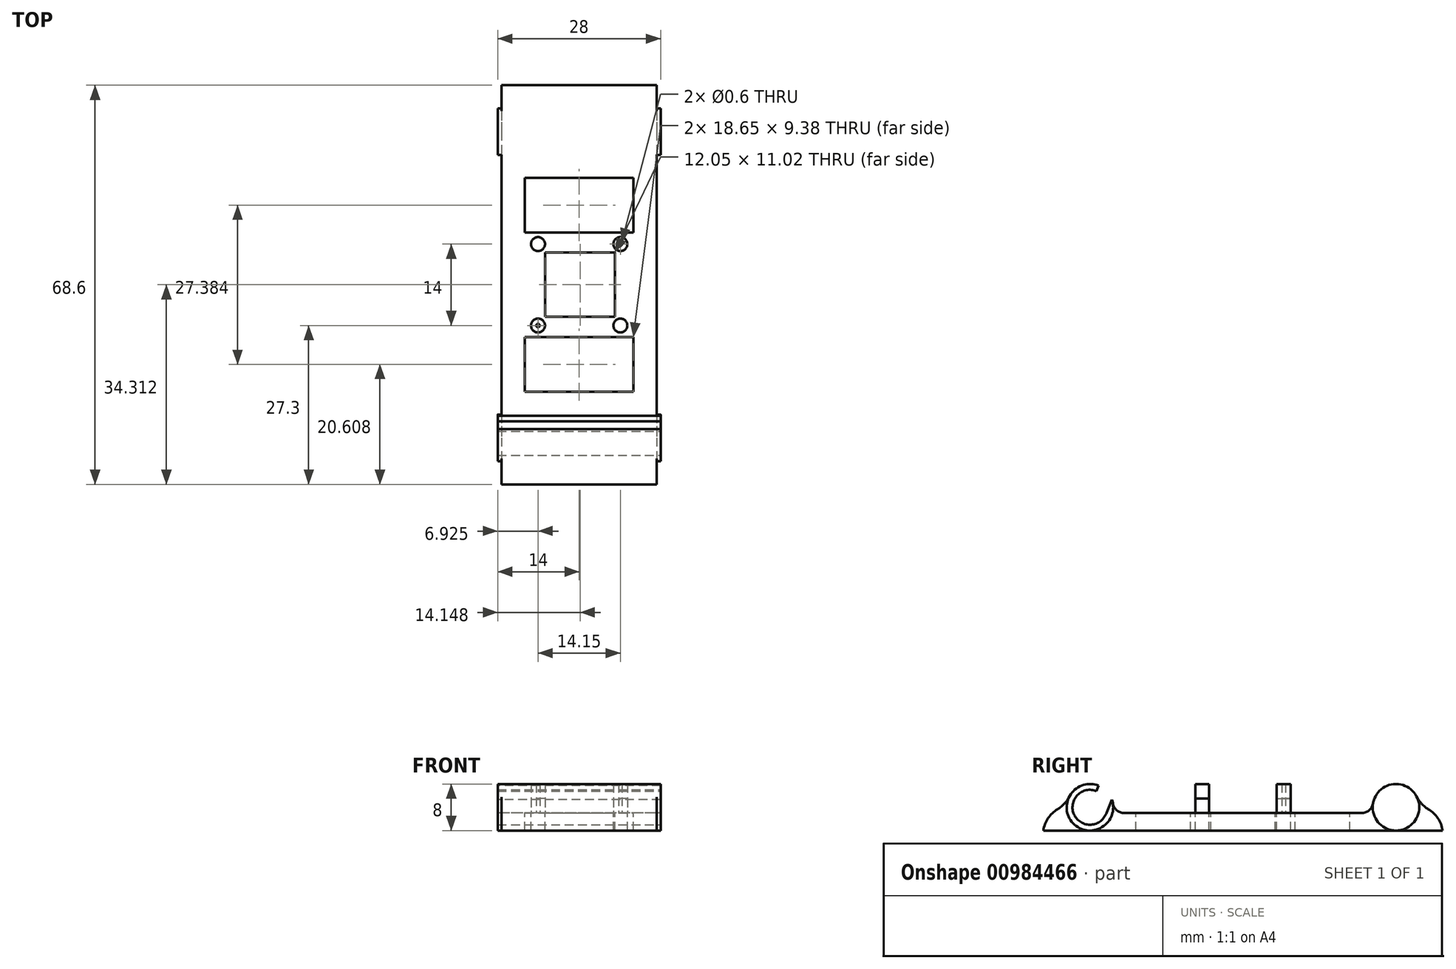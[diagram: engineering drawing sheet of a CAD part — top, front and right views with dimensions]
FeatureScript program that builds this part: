
annotation { "Feature Type Name" : "Feature", "Feature Type Description" : "" }
export const myFeature = defineFeature(function(context is Context, id is Id, definition is map)
    precondition{}
    {
        {
            var Q0;
            Q0=qCreatedBy(makeId("Top.planeOp"),FACE);
            var sketch = newSketch(context, id + "F0", { "sketchPlane" : qUnion([Q0])});
            skCircle(sketch, "E0", {"center": v(7.08, 7) * mm, "radius": 1.2 * mm});
            skLineSegment(sketch, "E1", {"start": v(7.08, 7) * mm, "end": v(-7.08, 7) * mm, "construction": true});
            skCircle(sketch, "E2", {"center": v(-7.07, -7) * mm, "radius": 1.2 * mm});
            skLineSegment(sketch, "E3", {"start": v(7.08, 7) * mm, "end": v(7.08, -7) * mm, "construction": true});
            skLineSegment(sketch, "E4", {"start": v(-7.08, 7) * mm, "end": v(-7.08, -7) * mm, "construction": true});
            skLineSegment(sketch, "E5", {"start": v(-7.07, -7) * mm, "end": v(7.08, -7) * mm, "construction": true});
            skSolve(sketch);
        }
        {
            var Q0;
            Q0 = qSketchRegion(id + "F0", true);
            extrude(context, id + "F1", {"entities" : qUnion([Q0]), "depth" : 5 * mm, "offsetDistance" : 25 * mm});
        }
        {
            var Q0;
            Q0=qCreatedBy(makeId("Top.planeOp"),FACE);
            var sketch = newSketch(context, id + "F2", { "sketchPlane" : qUnion([Q0])});
            skCircle(sketch, "E6", {"center": v(-7.08, -7) * mm, "radius": 0.3 * mm});
            skCircle(sketch, "E7", {"center": v(7.08, 7) * mm, "radius": 0.3 * mm});
            skSolve(sketch);
        }
        {
            var Q0;
            Q0 = qSketchRegion(id + "F2", true);
            extrude(context, id + "F3", {"entities" : qUnion([Q0]), "operationType" : NewBodyOperationType.REMOVE, "depth" : 5 * mm, "offsetDistance" : 25 * mm});
        }
        {
            var Q0;
            Q0=qCreatedBy(makeId("Top.planeOp"),FACE);
            var sketch = newSketch(context, id + "F4", { "sketchPlane" : qUnion([Q0])});
            skLineSegment(sketch, "E8", {"start": v(-8.33, -8.25) * mm, "end": v(-8.33, 8.25) * mm});
            skLineSegment(sketch, "E9", {"start": v(-8.33, 8.25) * mm, "end": v(8.32, 8.25) * mm});
            skLineSegment(sketch, "E10", {"start": v(8.33, -8.25) * mm, "end": v(-8.32, -8.25) * mm});
            skLineSegment(sketch, "E11", {"start": v(8.33, -8.25) * mm, "end": v(8.33, 8.25) * mm});
            skLineSegment(sketch, "E12.bottom", {"start": v(-5.88, -5.5) * mm, "end": v(6.17, -5.5) * mm});
            skLineSegment(sketch, "E12.top", {"start": v(-5.88, 5.52) * mm, "end": v(6.17, 5.52) * mm});
            skLineSegment(sketch, "E12.left", {"start": v(-5.88, -5.5) * mm, "end": v(-5.88, 5.52) * mm});
            skLineSegment(sketch, "E12.right", {"start": v(6.17, -5.5) * mm, "end": v(6.17, 5.52) * mm});
            skSolve(sketch);
        }
        {
            var Q0;
            Q0 = qSketchRegion(id + "F4", true);
            extrude(context, id + "F5", {"entities" : qUnion([Q0]), "oppositeDirection" : true, "depth" : 3 * mm, "offsetDistance" : 25 * mm});
        }
        {
            var Q0;
            Q0 = qSketchRegion(id + "F0", true);
            extrude(context, id + "F6", {"entities" : qUnion([Q0]), "oppositeDirection" : true, "depth" : 3 * mm, "offsetDistance" : 25 * mm});
        }
        {
            var Q0;
            Q0=qCreatedBy(makeId("Top.planeOp"),FACE);
            var sketch = newSketch(context, id + "F7", { "sketchPlane" : qUnion([Q0])});
            skCircle(sketch, "E13", {"center": v(-7.08, 7) * mm, "radius": 1.2 * mm});
            skCircle(sketch, "E14", {"center": v(7.08, -7) * mm, "radius": 1.2 * mm});
            skSolve(sketch);
        }
        {
            var Q0;
            Q0 = qSketchRegion(id + "F7", true);
            extrude(context, id + "F8", {"entities" : qUnion([Q0]), "operationType" : NewBodyOperationType.ADD, "depth" : 2.5 * mm, "offsetDistance" : 25 * mm});
        }
        {
            var Q0;
            Q0=qCreatedBy(makeId("Top.planeOp"),FACE);
            var sketch = newSketch(context, id + "F9", { "sketchPlane" : qUnion([Q0])});
            skLineSegment(sketch, "E15.bottom", {"start": v(-8.33, 8.25) * mm, "end": v(8.32, 8.25) * mm});
            skLineSegment(sketch, "E15.top", {"start": v(-8.33, 26.3) * mm, "end": v(8.33, 26.3) * mm, "construction": true});
            skLineSegment(sketch, "E16.bottom", {"start": v(-8.33, -8.25) * mm, "end": v(8.33, -8.25) * mm});
            skLineSegment(sketch, "E17.left", {"start": v(8.32, 8.25) * mm, "end": v(8.32, -8.25) * mm});
            skLineSegment(sketch, "E17.right", {"start": v(13.33, 34.3) * mm, "end": v(13.33, -34.3) * mm});
            skLineSegment(sketch, "E18.right", {"start": v(-13.33, 34.3) * mm, "end": v(-13.32, -34.3) * mm});
            skLineSegment(sketch, "E19", {"start": v(-8.33, 8.25) * mm, "end": v(-8.33, -8.25) * mm});
            skLineSegment(sketch, "E20", {"start": v(-13.33, 34.3) * mm, "end": v(13.33, 34.3) * mm});
            skLineSegment(sketch, "E21", {"start": v(-8.33, -26.3) * mm, "end": v(7.82, -26.3) * mm, "construction": true});
            skLineSegment(sketch, "E22", {"start": v(-13.32, -34.3) * mm, "end": v(13.33, -34.3) * mm});
            skSolve(sketch);
        }
        {
            var Q0;
            Q0 = qSketchRegion(id + "F9", true);
            extrude(context, id + "F10", {"entities" : qUnion([Q0]), "operationType" : NewBodyOperationType.ADD, "oppositeDirection" : true, "depth" : 3 * mm, "offsetDistance" : 25 * mm});
        }
        {
            var Q0;
            Q0=qCreatedBy(makeId("Right.planeOp"),FACE);
            var sketch = newSketch(context, id + "F11", { "sketchPlane" : qUnion([Q0])});
            skLineSegment(sketch, "E23", {"start": v(-26.3, 1) * mm, "end": v(-26.3, 0) * mm, "construction": true});
            skCircle(sketch, "E24", {"center": v(-26.3, 1) * mm, "radius": 4 * mm});
            skLineSegment(sketch, "E25", {"start": v(26.3, 1) * mm, "end": v(26.3, 0) * mm, "construction": true});
            skCircle(sketch, "E26", {"center": v(26.3, 1) * mm, "radius": 4 * mm});
            skSolve(sketch);
        }
        {
            var Q0;
            Q0 = qSketchRegion(id + "F11", true);
            extrude(context, id + "F12", {"entities" : qUnion([Q0]), "operationType" : NewBodyOperationType.ADD, "depth" : 14 * mm, "offsetDistance" : 25 * mm, "hasSecondDirection" : true, "secondDirectionOppositeDirection" : true, "secondDirectionDepth" : 14 * mm});
        }
        {
            var Q0;
            Q0=qCreatedBy(makeId("Right.planeOp"),FACE);
            var sketch = newSketch(context, id + "F13", { "sketchPlane" : qUnion([Q0])});
            skArc(sketch, "E27", {"start": v(-25.17, 3.78) * mm, "mid": v(-29.01, -0.28) * mm, "end": v(-23.44, 0.11) * mm});
            skLineSegment(sketch, "E28", {"start": v(-26.3, 1) * mm, "end": v(-26.3, 0) * mm, "construction": true});
            skLineSegment(sketch, "E29", {"start": v(-24.4, 5.63) * mm, "end": v(-21.63, 4.48) * mm});
            skLineSegment(sketch, "E30", {"start": v(-21.63, 4.48) * mm, "end": v(-23.44, 0.11) * mm});
            skLineSegment(sketch, "E31", {"start": v(-24.4, 5.63) * mm, "end": v(-25.17, 3.78) * mm});
            skSolve(sketch);
        }
        {
            var Q0;
            Q0 = qSketchRegion(id + "F13", true);
            extrude(context, id + "F14", {"entities" : qUnion([Q0]), "operationType" : NewBodyOperationType.REMOVE, "oppositeDirection" : true, "depth" : 14 * mm, "offsetDistance" : 25 * mm, "hasSecondDirection" : true, "secondDirectionOppositeDirection" : false, "secondDirectionDepth" : 14 * mm});
        }
        {
            var Q0;
            Q0=makeQuery(id+"F12.boolean.opBoolean","INTERSECT",EDGE,{"disambiguationData":[OD(0.0)],"derivedFrom":[makeQuery(id+"F10.boolean.opBoolean","MERGE",FACE,{"derivedFrom":[makeQuery(id+"F5.opExtrude","CAP_FACE",FACE,{"disambiguationData":[OSD([sQuery(id+"F4.wireOp",EDGE,"E8"),sQuery(id+"F4.wireOp",EDGE,"E9"),sQuery(id+"F4.wireOp",EDGE,"E10"),sQuery(id+"F4.wireOp",EDGE,"E11"),sQuery(id+"F4.wireOp",EDGE,"E12.bottom"),sQuery(id+"F4.wireOp",EDGE,"E12.top"),sQuery(id+"F4.wireOp",EDGE,"E12.left"),sQuery(id+"F4.wireOp",EDGE,"E12.right")])],"isStart":true}),makeQuery(id+"F10.opExtrude","CAP_FACE",FACE,{"disambiguationData":[OSD([sQuery(id+"F9.wireOp",EDGE,"E15.bottom"),sQuery(id+"F9.wireOp",EDGE,"E16.bottom"),sQuery(id+"F9.wireOp",EDGE,"E17.left"),sQuery(id+"F9.wireOp",EDGE,"E17.right"),sQuery(id+"F9.wireOp",EDGE,"E18.right"),sQuery(id+"F9.wireOp",EDGE,"E19"),sQuery(id+"F9.wireOp",EDGE,"E20"),sQuery(id+"F9.wireOp",EDGE,"E22")])],"isStart":true})]}),makeQuery(id+"F12.opExtrude","SWEPT_FACE",FACE,{"disambiguationData":[OSD([sQuery(id+"F11.wireOp",EDGE,"E24")])]})]});
            var Q1;
            Q1=makeQuery(id+"F12.boolean.opBoolean","INTERSECT",EDGE,{"disambiguationData":[OD(0.0)],"derivedFrom":[makeQuery(id+"F10.boolean.opBoolean","MERGE",FACE,{"derivedFrom":[makeQuery(id+"F5.opExtrude","CAP_FACE",FACE,{"disambiguationData":[OSD([sQuery(id+"F4.wireOp",EDGE,"E8"),sQuery(id+"F4.wireOp",EDGE,"E9"),sQuery(id+"F4.wireOp",EDGE,"E10"),sQuery(id+"F4.wireOp",EDGE,"E11"),sQuery(id+"F4.wireOp",EDGE,"E12.bottom"),sQuery(id+"F4.wireOp",EDGE,"E12.top"),sQuery(id+"F4.wireOp",EDGE,"E12.left"),sQuery(id+"F4.wireOp",EDGE,"E12.right")])],"isStart":true}),makeQuery(id+"F10.opExtrude","CAP_FACE",FACE,{"disambiguationData":[OSD([sQuery(id+"F9.wireOp",EDGE,"E15.bottom"),sQuery(id+"F9.wireOp",EDGE,"E16.bottom"),sQuery(id+"F9.wireOp",EDGE,"E17.left"),sQuery(id+"F9.wireOp",EDGE,"E17.right"),sQuery(id+"F9.wireOp",EDGE,"E18.right"),sQuery(id+"F9.wireOp",EDGE,"E19"),sQuery(id+"F9.wireOp",EDGE,"E20"),sQuery(id+"F9.wireOp",EDGE,"E22")])],"isStart":true})]}),makeQuery(id+"F12.opExtrude","SWEPT_FACE",FACE,{"disambiguationData":[OSD([sQuery(id+"F11.wireOp",EDGE,"E26")])]})]});
            fillet(context, id + "F15", {"entities" : qUnion([Q0, Q1]), "radius" : 5 * mm, "tangentPropagation" : true, "allowEdgeOverflow" : false});
        }
        {
            var Q0;
            Q0=makeQuery(id+"F12.boolean.opBoolean","INTERSECT",EDGE,{"disambiguationData":[OD(1.0)],"derivedFrom":[makeQuery(id+"F10.boolean.opBoolean","MERGE",FACE,{"derivedFrom":[makeQuery(id+"F5.opExtrude","CAP_FACE",FACE,{"disambiguationData":[OSD([sQuery(id+"F4.wireOp",EDGE,"E8"),sQuery(id+"F4.wireOp",EDGE,"E9"),sQuery(id+"F4.wireOp",EDGE,"E10"),sQuery(id+"F4.wireOp",EDGE,"E11"),sQuery(id+"F4.wireOp",EDGE,"E12.bottom"),sQuery(id+"F4.wireOp",EDGE,"E12.top"),sQuery(id+"F4.wireOp",EDGE,"E12.left"),sQuery(id+"F4.wireOp",EDGE,"E12.right")])],"isStart":true}),makeQuery(id+"F10.opExtrude","CAP_FACE",FACE,{"disambiguationData":[OSD([sQuery(id+"F9.wireOp",EDGE,"E15.bottom"),sQuery(id+"F9.wireOp",EDGE,"E16.bottom"),sQuery(id+"F9.wireOp",EDGE,"E17.left"),sQuery(id+"F9.wireOp",EDGE,"E17.right"),sQuery(id+"F9.wireOp",EDGE,"E18.right"),sQuery(id+"F9.wireOp",EDGE,"E19"),sQuery(id+"F9.wireOp",EDGE,"E20"),sQuery(id+"F9.wireOp",EDGE,"E22")])],"isStart":true})]}),makeQuery(id+"F12.opExtrude","SWEPT_FACE",FACE,{"disambiguationData":[OSD([sQuery(id+"F11.wireOp",EDGE,"E24")])]})]});
            var Q1;
            Q1=makeQuery(id+"F12.boolean.opBoolean","INTERSECT",EDGE,{"disambiguationData":[OD(1.0)],"derivedFrom":[makeQuery(id+"F10.boolean.opBoolean","MERGE",FACE,{"derivedFrom":[makeQuery(id+"F5.opExtrude","CAP_FACE",FACE,{"disambiguationData":[OSD([sQuery(id+"F4.wireOp",EDGE,"E8"),sQuery(id+"F4.wireOp",EDGE,"E9"),sQuery(id+"F4.wireOp",EDGE,"E10"),sQuery(id+"F4.wireOp",EDGE,"E11"),sQuery(id+"F4.wireOp",EDGE,"E12.bottom"),sQuery(id+"F4.wireOp",EDGE,"E12.top"),sQuery(id+"F4.wireOp",EDGE,"E12.left"),sQuery(id+"F4.wireOp",EDGE,"E12.right")])],"isStart":true}),makeQuery(id+"F10.opExtrude","CAP_FACE",FACE,{"disambiguationData":[OSD([sQuery(id+"F9.wireOp",EDGE,"E15.bottom"),sQuery(id+"F9.wireOp",EDGE,"E16.bottom"),sQuery(id+"F9.wireOp",EDGE,"E17.left"),sQuery(id+"F9.wireOp",EDGE,"E17.right"),sQuery(id+"F9.wireOp",EDGE,"E18.right"),sQuery(id+"F9.wireOp",EDGE,"E19"),sQuery(id+"F9.wireOp",EDGE,"E20"),sQuery(id+"F9.wireOp",EDGE,"E22")])],"isStart":true})]}),makeQuery(id+"F12.opExtrude","SWEPT_FACE",FACE,{"disambiguationData":[OSD([sQuery(id+"F11.wireOp",EDGE,"E26")])]})]});
            fillet(context, id + "F16", {"entities" : qUnion([Q0, Q1]), "radius" : 2 * mm, "tangentPropagation" : true, "allowEdgeOverflow" : false});
        }
        {
            var Q0;
            Q0=qCreatedBy(makeId("Top.planeOp"),FACE);
            var sketch = newSketch(context, id + "F17", { "sketchPlane" : qUnion([Q0])});
            skLineSegment(sketch, "E32.bottom", {"start": v(-9.33, 18.38) * mm, "end": v(9.33, 18.38) * mm});
            skLineSegment(sketch, "E32.top", {"start": v(-9.33, 9) * mm, "end": v(9.33, 9) * mm});
            skLineSegment(sketch, "E32.left", {"start": v(-9.33, 18.38) * mm, "end": v(-9.33, 9) * mm});
            skLineSegment(sketch, "E32.right", {"start": v(9.33, 18.38) * mm, "end": v(9.33, 9) * mm});
            skLineSegment(sketch, "E33.bottom", {"start": v(-9.32, -9) * mm, "end": v(9.33, -9) * mm});
            skLineSegment(sketch, "E33.top", {"start": v(-9.32, -18.38) * mm, "end": v(9.33, -18.38) * mm});
            skLineSegment(sketch, "E33.left", {"start": v(-9.32, -9) * mm, "end": v(-9.32, -18.38) * mm});
            skLineSegment(sketch, "E33.right", {"start": v(9.33, -9) * mm, "end": v(9.33, -18.38) * mm});
            skSolve(sketch);
        }
        {
            var Q0;
            Q0 = qSketchRegion(id + "F17", true);
            extrude(context, id + "F18", {"entities" : qUnion([Q0]), "operationType" : NewBodyOperationType.REMOVE, "oppositeDirection" : true, "depth" : 3 * mm, "offsetDistance" : 25 * mm});
        }
        {
            var Q0;
            {var subQ0=sQuery(id+"F9.wireOp",EDGE,"E20");Q0=makeQuery(id+"F15.opFillet","BLEND_EDGE",EDGE,{"blendedFrom":[makeQuery(id+"F12.boolean.opBoolean","INTERSECT",EDGE,{"disambiguationData":[OD(0.0)],"derivedFrom":[makeQuery(id+"F10.boolean.opBoolean","MERGE",FACE,{"derivedFrom":[makeQuery(id+"F5.opExtrude","CAP_FACE",FACE,{"disambiguationData":[OSD([sQuery(id+"F4.wireOp",EDGE,"E8"),sQuery(id+"F4.wireOp",EDGE,"E9"),sQuery(id+"F4.wireOp",EDGE,"E10"),sQuery(id+"F4.wireOp",EDGE,"E11"),sQuery(id+"F4.wireOp",EDGE,"E12.bottom"),sQuery(id+"F4.wireOp",EDGE,"E12.top"),sQuery(id+"F4.wireOp",EDGE,"E12.left"),sQuery(id+"F4.wireOp",EDGE,"E12.right")])],"isStart":true}),makeQuery(id+"F10.opExtrude","CAP_FACE",FACE,{"disambiguationData":[OSD([sQuery(id+"F9.wireOp",EDGE,"E15.bottom"),sQuery(id+"F9.wireOp",EDGE,"E16.bottom"),sQuery(id+"F9.wireOp",EDGE,"E17.left"),sQuery(id+"F9.wireOp",EDGE,"E17.right"),sQuery(id+"F9.wireOp",EDGE,"E18.right"),sQuery(id+"F9.wireOp",EDGE,"E19"),subQ0,sQuery(id+"F9.wireOp",EDGE,"E22")])],"isStart":true})]}),makeQuery(id+"F12.opExtrude","SWEPT_FACE",FACE,{"disambiguationData":[OSD([sQuery(id+"F11.wireOp",EDGE,"E26")])]})]}),makeQuery(id+"F10.opExtrude","SWEPT_FACE",FACE,{"disambiguationData":[OSD([subQ0])]})],"blendedInto":[makeQuery(id+"F10.opExtrude","SWEPT_FACE",FACE,{"disambiguationData":[OSD([subQ0])]})]});}
            var Q1;
            {var subQ0=sQuery(id+"F9.wireOp",EDGE,"E22");Q1=makeQuery(id+"F15.opFillet","BLEND_EDGE",EDGE,{"blendedFrom":[makeQuery(id+"F12.boolean.opBoolean","INTERSECT",EDGE,{"disambiguationData":[OD(0.0)],"derivedFrom":[makeQuery(id+"F10.boolean.opBoolean","MERGE",FACE,{"derivedFrom":[makeQuery(id+"F5.opExtrude","CAP_FACE",FACE,{"disambiguationData":[OSD([sQuery(id+"F4.wireOp",EDGE,"E8"),sQuery(id+"F4.wireOp",EDGE,"E9"),sQuery(id+"F4.wireOp",EDGE,"E10"),sQuery(id+"F4.wireOp",EDGE,"E11"),sQuery(id+"F4.wireOp",EDGE,"E12.bottom"),sQuery(id+"F4.wireOp",EDGE,"E12.top"),sQuery(id+"F4.wireOp",EDGE,"E12.left"),sQuery(id+"F4.wireOp",EDGE,"E12.right")])],"isStart":true}),makeQuery(id+"F10.opExtrude","CAP_FACE",FACE,{"disambiguationData":[OSD([sQuery(id+"F9.wireOp",EDGE,"E15.bottom"),sQuery(id+"F9.wireOp",EDGE,"E16.bottom"),sQuery(id+"F9.wireOp",EDGE,"E17.left"),sQuery(id+"F9.wireOp",EDGE,"E17.right"),sQuery(id+"F9.wireOp",EDGE,"E18.right"),sQuery(id+"F9.wireOp",EDGE,"E19"),sQuery(id+"F9.wireOp",EDGE,"E20"),subQ0])],"isStart":true})]}),makeQuery(id+"F12.opExtrude","SWEPT_FACE",FACE,{"disambiguationData":[OSD([sQuery(id+"F11.wireOp",EDGE,"E24")])]})]}),makeQuery(id+"F10.opExtrude","SWEPT_FACE",FACE,{"disambiguationData":[OSD([subQ0])]})],"blendedInto":[makeQuery(id+"F10.opExtrude","SWEPT_FACE",FACE,{"disambiguationData":[OSD([subQ0])]})]});}
            fillet(context, id + "F19", {"entities" : qUnion([Q0, Q1]), "radius" : 5 * mm, "tangentPropagation" : true, "allowEdgeOverflow" : false});
        }
    });
